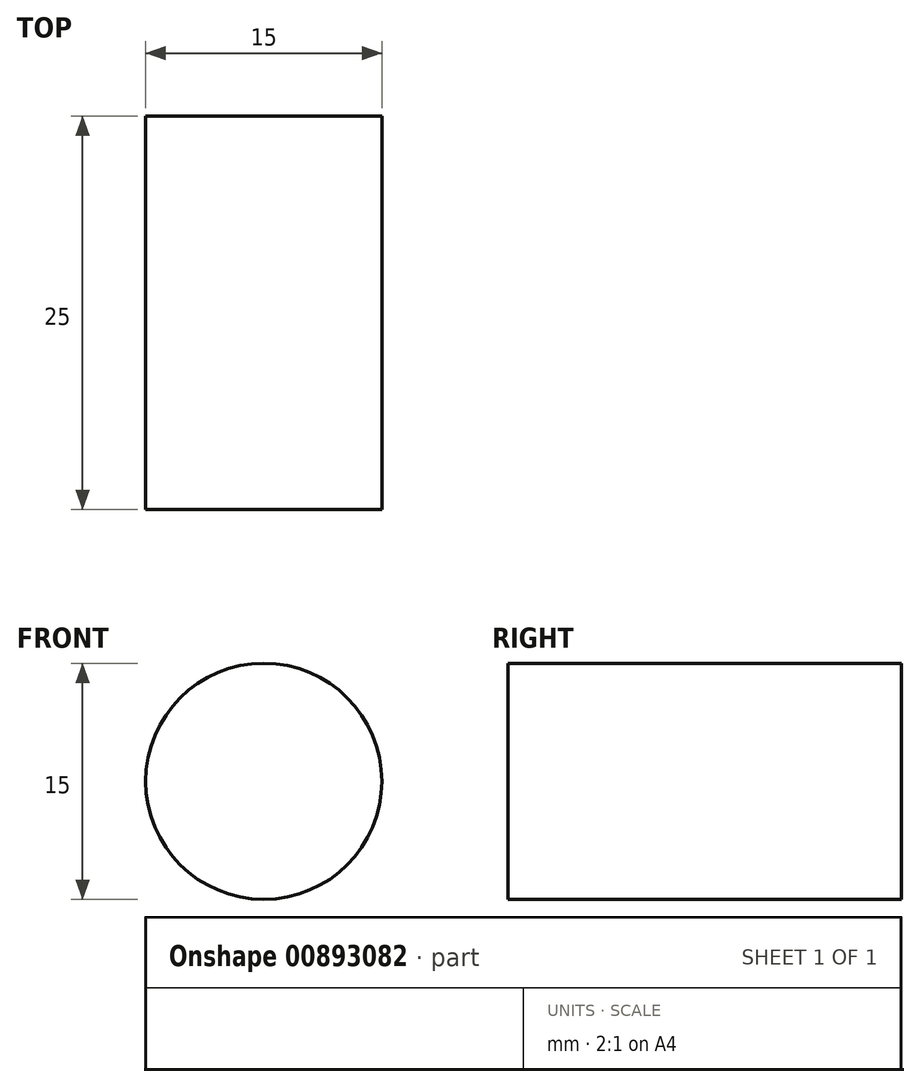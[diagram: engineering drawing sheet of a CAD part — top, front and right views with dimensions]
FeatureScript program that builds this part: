
annotation { "Feature Type Name" : "Feature", "Feature Type Description" : "" }
export const myFeature = defineFeature(function(context is Context, id is Id, definition is map)
    precondition{}
    {
        {
            var Q0;
            Q0=qCreatedBy(makeId("Front.planeOp"),FACE);
            var sketch = newSketch(context, id + "F0", { "sketchPlane" : qUnion([Q0])});
            skCircle(sketch, "E0", {"center": v(0, 0) * mm, "radius": 7.5 * mm});
            skSolve(sketch);
        }
        {
            var Q0;
            Q0 = qSketchRegion(id + "F0", true);
            extrude(context, id + "F1", {"entities" : qUnion([Q0]), "depth" : 25 * mm, "offsetDistance" : 25 * mm});
        }
    });
